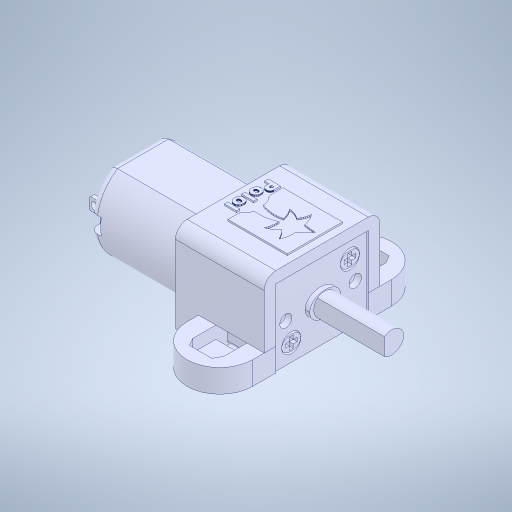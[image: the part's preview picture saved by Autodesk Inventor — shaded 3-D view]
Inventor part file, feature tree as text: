
AUTODESK INVENTOR PART (.ipt)
format: ipt  version: 2023.2 (Build 272271000, 271)  size: 915,968 bytes
history: mixed  units: in
note: dims shown in document units (in); Inventor stores cm internally (conversion verified against a paired STEP export)
features: other x1, fillet x1, imported_body x1
ambient origin geometry x8: Origin, YZ Plane, XZ Plane, XY Plane, X Axis, Y Axis, Z Axis, Center Point
bodies: Solid1 (imported_parasolid)
feature tree (3):
  other  "Plane1"
  fillet  "Fillet3"  [1 undecoded]
  imported_body  NMx_Import_Brep_tag  [imported B-rep: ~8 faces, bbox_mm=None]
note: 1 required parameter value undecoded (feature->parameter linkage not recoverable at this tier; creation-order binding heuristic only, values carry confidence <= 0.55)
